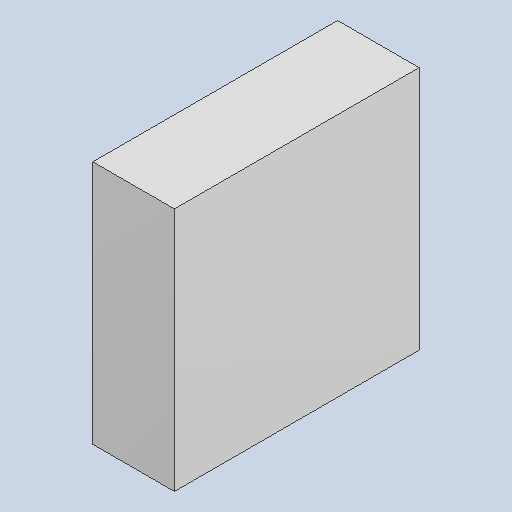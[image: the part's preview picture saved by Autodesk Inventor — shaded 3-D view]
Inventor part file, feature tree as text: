
AUTODESK INVENTOR PART (.ipt)
format: ipt  version: 2023.4 (Build 274418000, 418)  size: 81,408 bytes
history: native  units: mm
features: extrude x1
ambient origin geometry x8: Origin, YZ Plane, XZ Plane, XY Plane, X Axis, Y Axis, Z Axis, Center Point
bodies: Solid1 (feature_tree)
feature tree (1):
  extrude  "Extruded_45"  [1 undecoded]
note: 1 required parameter value undecoded (feature->parameter linkage not recoverable at this tier; creation-order binding heuristic only, values carry confidence <= 0.55)
